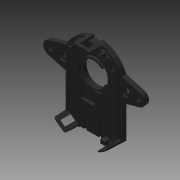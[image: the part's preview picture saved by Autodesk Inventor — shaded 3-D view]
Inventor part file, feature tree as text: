
AUTODESK INVENTOR PART (.ipt)
format: ipt  version: 2018 (Build 220112000, 112)  size: 1,541,632 bytes
history: native  units: in
note: dims shown in document units (in); Inventor stores cm internally (conversion verified against a paired STEP export)
features: projected_geometry x27, extrude x11, sketch x11, other x1
ambient origin geometry x8: Origin, YZ Plane, XZ Plane, XY Plane, X Axis, Y Axis, Z Axis, Center Point
bodies: Solid1 (feature_tree)
feature tree (50):
  other  "amt102-v"
  extrude  "Extrusion1"  Depth=0.0394in TaperAngle=0.0deg
  extrude  "Extrusion2"  Depth=0.1481in TaperAngle=0.0deg
  sketch  "Sketch3"  dims[d8=0.1063in d9=0.0in d10=0.0438in d11=0.0in]
  extrude  "Extrusion3"  Depth=0.0438in TaperAngle=0.0deg
  sketch  "Sketch4"  dims[d12=0.3937in d13=0.0in d14=0.3937in d15=0.0in]
  extrude  "Extrusion4"  Depth=0.3937in TaperAngle=0.0deg
  extrude  "Extrusion5"  Depth=1.2768in
  sketch  "Sketch5"  dims[d16=0.0394in d17=0.0in d18=1.2768in]
  extrude  "Extrusion6"  Depth=2.0669in
  extrude  "Extrusion7"  Depth=0.113in
  extrude  "Extrusion8"  Depth=0.1181in
  extrude  "Extrusion9"  Depth=0.1969in
  extrude  "Extrusion10"  Depth=0.0394in TaperAngle=0.0deg
  extrude  "Extrusion11"  [1 undecoded]
  sketch  "Sketch1"  dims[d0=0.0438in d1=0.0in d2=0.0394in d3=0.0in]
  projected_geometry  "Projected Loop1"
  projected_geometry  "Projected Loop2"
  projected_geometry  "Projected Loop3"
  projected_geometry  "Projected Loop4"
  projected_geometry  "Projected Loop5"
  projected_geometry  "Projected Loop6"
  projected_geometry  "Projected Loop7"
  projected_geometry  "Projected Loop8"
  projected_geometry  "Projected Loop9"
  sketch  "Sketch2"  dims[d4=0.0394in d5=0.0in d6=0.1481in d7=0.0in]
  projected_geometry  "Projected Loop10"
  projected_geometry  "Projected Loop11"
  projected_geometry  "Projected Loop12"
  projected_geometry  "Projected Loop13"
  projected_geometry  "Projected Loop14"
  projected_geometry  "Projected Loop15"
  projected_geometry  "Projected Loop16"
  projected_geometry  "Projected Loop17"
  projected_geometry  "Projected Loop18"
  projected_geometry  "Projected Loop19"
  sketch  "Sketch6"  dims[d19=1.812in d20=2.0669in]
  sketch  "Sketch7"  dims[d21=0.113in d22=0.113in]
  projected_geometry  "Projected Loop20"
  projected_geometry  "Projected Loop21"
  projected_geometry  "Projected Loop22"
  projected_geometry  "Projected Loop23"
  projected_geometry  "Projected Loop24"
  projected_geometry  "Projected Loop25"
  sketch  "Sketch8"  dims[d23=0.1181in d24=0.1181in]
  projected_geometry  "Projected Loop26"
  sketch  "Sketch9"  dims[d25=0.0984in d26=0.0227in d27=0.1969in]
  projected_geometry  "Projected Loop27"
  sketch  "Sketch10"  dims[d28=0.1969in d29=0.0394in d30=0.0in]
  sketch  "Sketch11"
note: 1 required parameter value undecoded (feature->parameter linkage not recoverable at this tier; creation-order binding heuristic only, values carry confidence <= 0.55)
